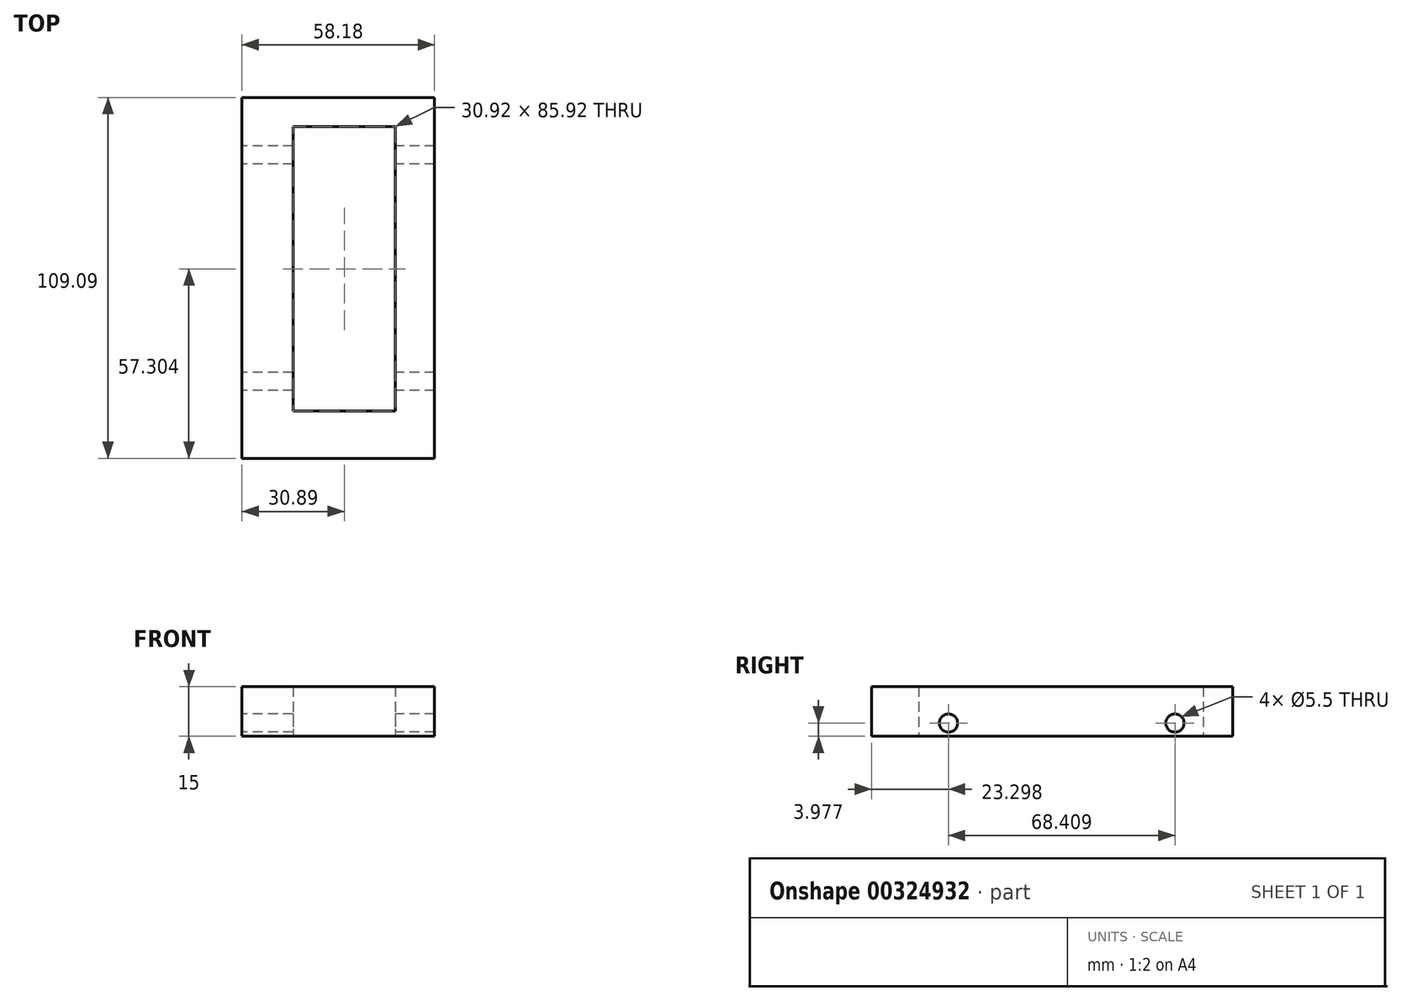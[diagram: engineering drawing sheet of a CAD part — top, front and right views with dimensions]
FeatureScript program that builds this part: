
annotation { "Feature Type Name" : "Feature", "Feature Type Description" : "" }
export const myFeature = defineFeature(function(context is Context, id is Id, definition is map)
    precondition{}
    {
        {
            var Q0;
            Q0=qCreatedBy(makeId("Top.planeOp"),FACE);
            var sketch = newSketch(context, id + "F0", { "sketchPlane" : qUnion([Q0])});
            skLineSegment(sketch, "E0.bottom", {"start": v(-38.18, 45.11) * mm, "end": v(20, 45.11) * mm});
            skLineSegment(sketch, "E0.top", {"start": v(-38.18, -63.98) * mm, "end": v(20, -63.98) * mm});
            skLineSegment(sketch, "E0.left", {"start": v(-38.18, 45.11) * mm, "end": v(-38.18, -63.98) * mm});
            skLineSegment(sketch, "E0.right", {"start": v(20, 45.11) * mm, "end": v(20, -63.98) * mm});
            skLineSegment(sketch, "E1.bottom", {"start": v(-22.75, -49.63) * mm, "end": v(8.17, -49.63) * mm});
            skLineSegment(sketch, "E1.top", {"start": v(-22.75, 36.28) * mm, "end": v(8.17, 36.28) * mm});
            skLineSegment(sketch, "E1.left", {"start": v(-22.75, -49.63) * mm, "end": v(-22.75, 36.28) * mm});
            skLineSegment(sketch, "E1.right", {"start": v(8.17, -49.63) * mm, "end": v(8.17, 36.28) * mm});
            skSolve(sketch);
        }
        {
            var Q0;
            Q0 = qSketchRegion(id + "F0", true);
            extrude(context, id + "F1", {"entities" : qUnion([Q0]), "depth" : 15 * mm});
        }
        {
            var Q0;
            Q0=makeQuery(id+"F1.opExtrude","SWEPT_FACE",FACE,{"disambiguationData":[OSD([sQuery(id+"F0.wireOp",EDGE,"E0.left")])]});
            var sketch = newSketch(context, id + "F2", { "sketchPlane" : qUnion([Q0])});
            skPoint(sketch, "E2", {"position": v(-27.73, 3.98) * mm});
            skPoint(sketch, "E3", {"position": v(40.68, 3.98) * mm});
            skSolve(sketch);
        }
        {
            var Q0;
            Q0=sQuery(id+"F2.wireOp",VERTEX,"E2");
            var Q1;
            Q1=sQuery(id+"F2.wireOp",VERTEX,"E3");
            var Q2;
            Q2=makeQuery(id+"F1.opExtrude","SWEPT_BODY",BODY,{"disambiguationData":[OSD([sQuery(id+"F0.wireOp",EDGE,"E0.bottom"),sQuery(id+"F0.wireOp",EDGE,"E0.top"),sQuery(id+"F0.wireOp",EDGE,"E0.left"),sQuery(id+"F0.wireOp",EDGE,"E0.right"),sQuery(id+"F0.wireOp",EDGE,"E1.bottom"),sQuery(id+"F0.wireOp",EDGE,"E1.top"),sQuery(id+"F0.wireOp",EDGE,"E1.left"),sQuery(id+"F0.wireOp",EDGE,"E1.right")])]});
            hole(context, id + "F3", {"style" : HoleStyle.SIMPLE, "endStyle" : HoleEndStyle.THROUGH, "holeDiameter" : 5.5 * mm, "tappedDepth" : 12 * mm, "tapClearance" : 3, "locations" : qUnion([Q0, Q1]), "scope" : qUnion([Q2])});
        }
    });
